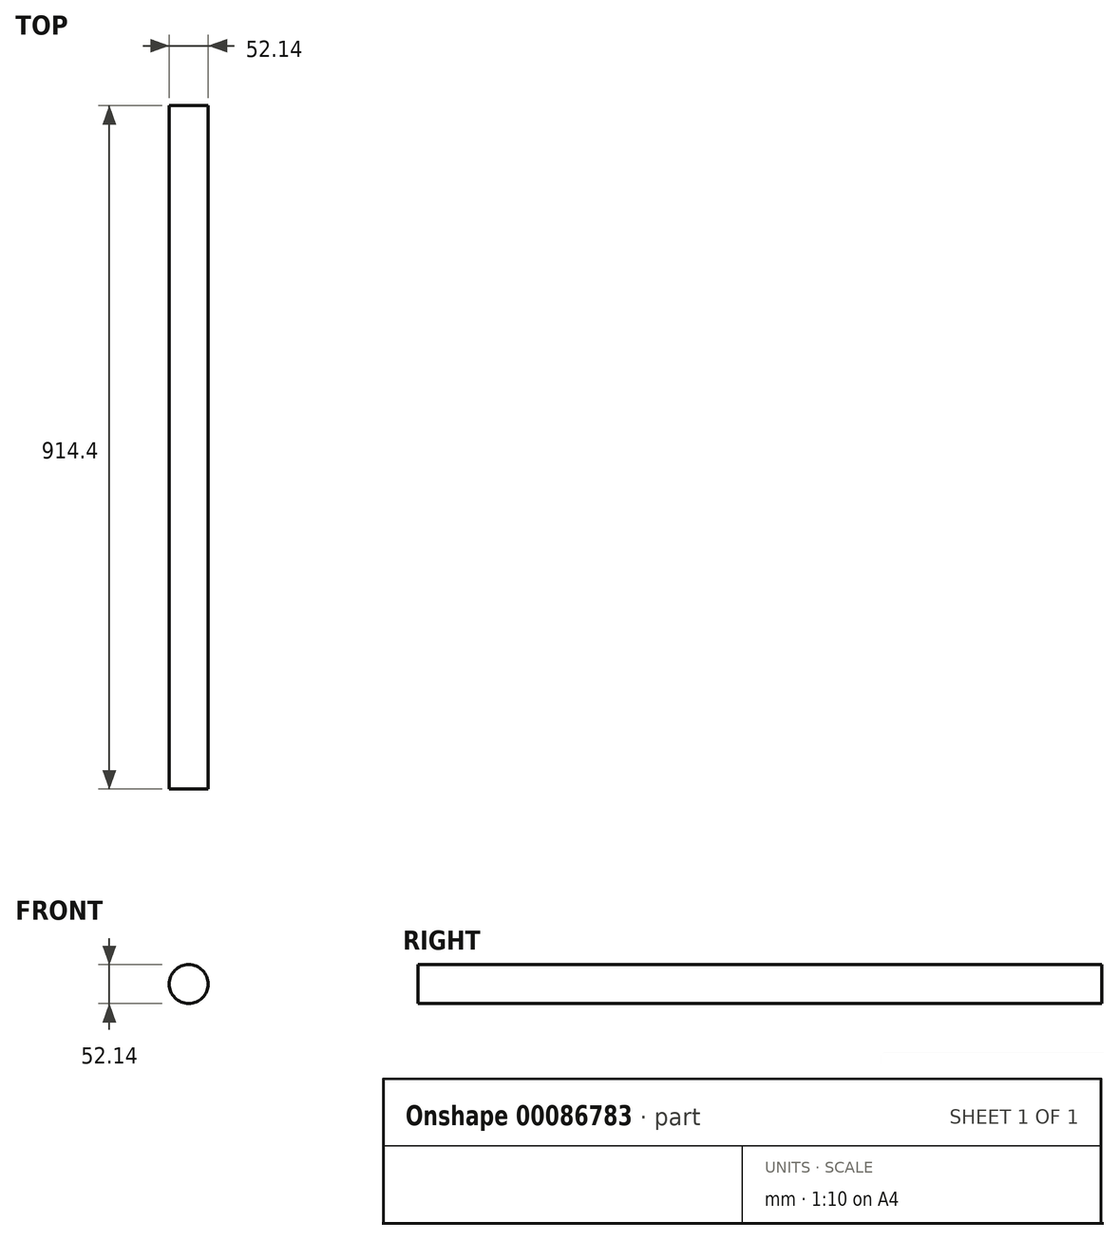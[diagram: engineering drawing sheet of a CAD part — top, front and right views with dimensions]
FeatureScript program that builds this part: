
annotation { "Feature Type Name" : "Feature", "Feature Type Description" : "" }
export const myFeature = defineFeature(function(context is Context, id is Id, definition is map)
    precondition{}
    {
        {
            var Q0;
            Q0=qCreatedBy(makeId("Front.planeOp"),FACE);
            var sketch = newSketch(context, id + "F0", { "sketchPlane" : qUnion([Q0])});
            skCircle(sketch, "E0", {"center": v(0, 0) * mm, "radius": 26.07 * mm});
            skSolve(sketch);
        }
        {
            var Q0;
            Q0 = qSketchRegion(id + "F0", true);
            extrude(context, id + "F1", {"entities" : qUnion([Q0]), "depth" : 914.4 * mm});
        }
    });
